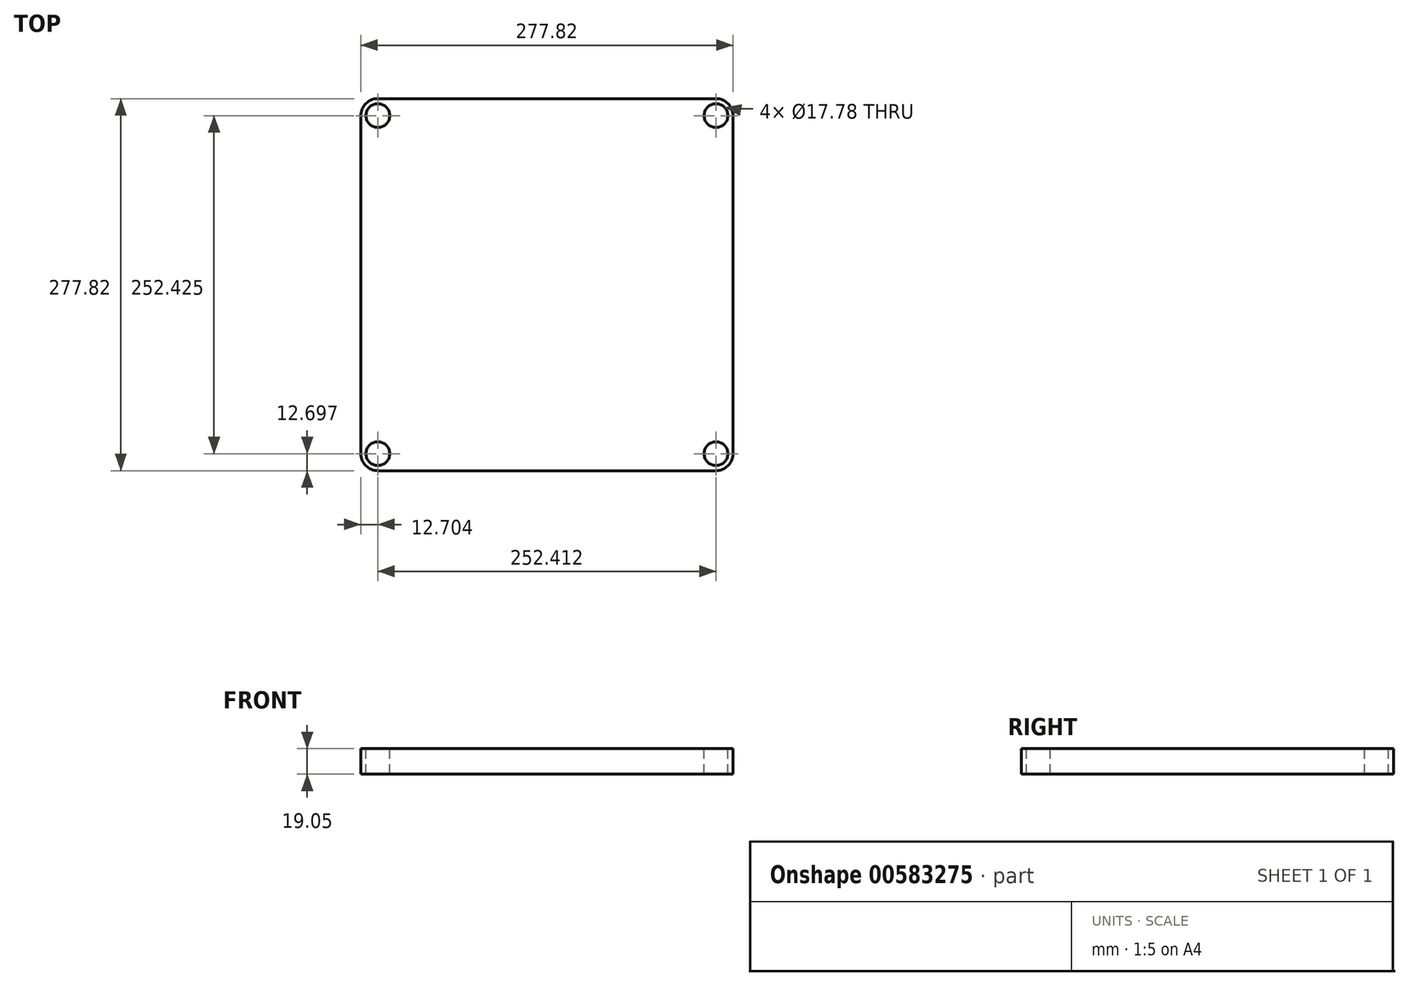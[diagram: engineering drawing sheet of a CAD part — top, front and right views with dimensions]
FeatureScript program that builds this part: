
annotation { "Feature Type Name" : "Feature", "Feature Type Description" : "" }
export const myFeature = defineFeature(function(context is Context, id is Id, definition is map)
    precondition{}
    {
        {
            var Q0;
            Q0=qCreatedBy(makeId("Top.planeOp"),FACE);
            var sketch = newSketch(context, id + "F0", { "sketchPlane" : qUnion([Q0])});
            skLineSegment(sketch, "E0.bottom", {"start": v(138.9, 138.91) * mm, "end": v(-138.9, 138.91) * mm});
            skLineSegment(sketch, "E0.top", {"start": v(138.9, -138.91) * mm, "end": v(-138.9, -138.91) * mm});
            skLineSegment(sketch, "E0.left", {"start": v(138.9, 138.91) * mm, "end": v(138.9, -138.91) * mm});
            skLineSegment(sketch, "E0.right", {"start": v(-138.9, 138.91) * mm, "end": v(-138.9, -138.91) * mm});
            skPoint(sketch, "E0.middle", {"position": v(0, 0) * mm});
            skSolve(sketch);
        }
        {
            var Q0;
            Q0=makeQuery(id+"F0.imprint","IMPRINT",FACE,{"disambiguationData":[TD([[makeQuery(id+"F0.imprint","IMPRINT",EDGE,{"derivedFrom":sQuery(id+"F0.wireOp",EDGE,"E0.bottom")}),1.0]])]});
            extrude(context, id + "F1", {"entities" : qUnion([Q0]), "depth" : 19.05 * mm, "offsetDistance" : 25.4 * mm});
        }
        {
            var Q0;
            Q0=makeQuery(id+"F1.opExtrude","SWEPT_EDGE",EDGE,{"disambiguationData":[OSD([sQuery(id+"F0.wireOp",EDGE,"E0.top"),sQuery(id+"F0.wireOp",EDGE,"E0.right")])]});
            var Q1;
            Q1=makeQuery(id+"F1.opExtrude","SWEPT_EDGE",EDGE,{"disambiguationData":[OSD([sQuery(id+"F0.wireOp",EDGE,"E0.bottom"),sQuery(id+"F0.wireOp",EDGE,"E0.right")])]});
            var Q2;
            Q2=makeQuery(id+"F1.opExtrude","SWEPT_EDGE",EDGE,{"disambiguationData":[OSD([sQuery(id+"F0.wireOp",EDGE,"E0.bottom"),sQuery(id+"F0.wireOp",EDGE,"E0.left")])]});
            var Q3;
            Q3=makeQuery(id+"F1.opExtrude","SWEPT_EDGE",EDGE,{"disambiguationData":[OSD([sQuery(id+"F0.wireOp",EDGE,"E0.top"),sQuery(id+"F0.wireOp",EDGE,"E0.left")])]});
            fillet(context, id + "F2", {"entities" : qUnion([Q0, Q1, Q2, Q3]), "radius" : 12.7 * mm, "tangentPropagation" : true, "allowEdgeOverflow" : false});
        }
        {
            var Q0;
            Q0=makeQuery(id+"F1.opExtrude","CAP_FACE",FACE,{"disambiguationData":[OSD([sQuery(id+"F0.wireOp",EDGE,"E0.bottom"),sQuery(id+"F0.wireOp",EDGE,"E0.top"),sQuery(id+"F0.wireOp",EDGE,"E0.left"),sQuery(id+"F0.wireOp",EDGE,"E0.right")])],"isStart":false});
            var sketch = newSketch(context, id + "F3", { "sketchPlane" : qUnion([Q0])});
            skCircle(sketch, "E1", {"center": v(-126.2, 126.21) * mm, "radius": 8.9 * mm});
            skCircle(sketch, "E2.MirrorC", {"center": v(126.2, 126.21) * mm, "radius": 8.9 * mm});
            skCircle(sketch, "E3.MirrorC", {"center": v(126.2, -126.21) * mm, "radius": 8.9 * mm});
            skCircle(sketch, "E4.MirrorC", {"center": v(-126.2, -126.21) * mm, "radius": 8.9 * mm});
            skSolve(sketch);
        }
        {
            var Q0;
            Q0 = qSketchRegion(id + "F3", true);
            extrude(context, id + "F4", {"entities" : qUnion([Q0]), "operationType" : NewBodyOperationType.REMOVE, "oppositeDirection" : true, "depth" : 25.4 * mm, "offsetDistance" : 25.4 * mm});
        }
    });
